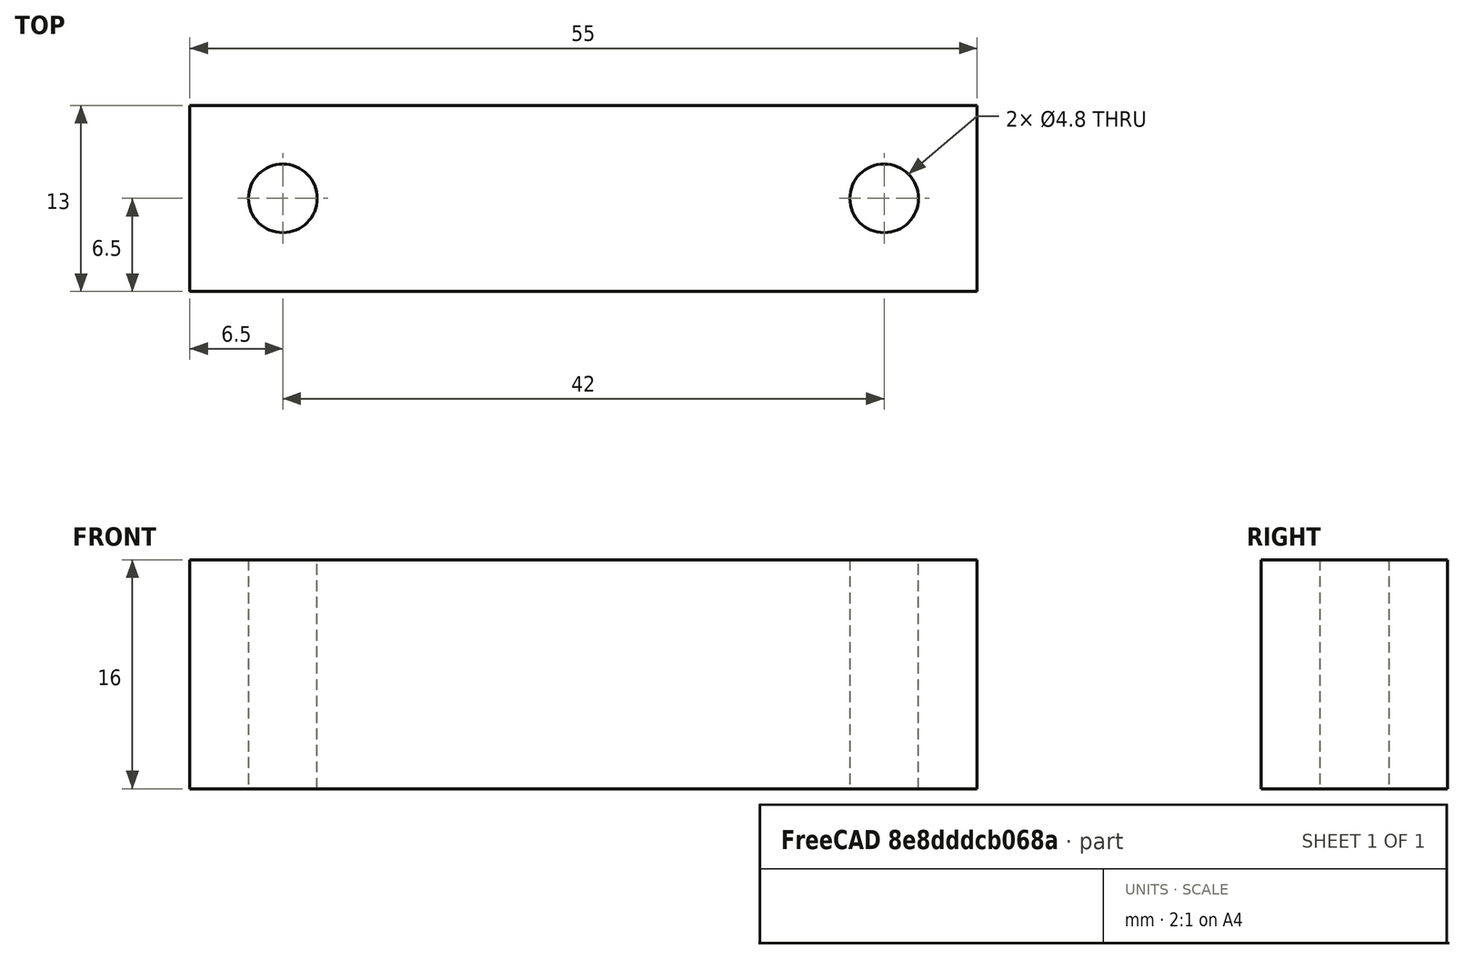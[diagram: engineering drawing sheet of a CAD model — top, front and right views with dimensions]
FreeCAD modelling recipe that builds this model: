
FCSTD DOCUMENT  (FreeCAD 0.16R6706 (Git))
Label: Calço Mancal Vertical
License: All rights reserved
LicenseURL: http://en.wikipedia.org/wiki/All_rights_reserved
objects: Sketcher::SketchObject×1, PartDesign::Pad×1
note: 3 computed .brp shape members not serialized (recipe doc carries the construction recipe); baked Part::Feature solids carry a one-line shape summary decoded from their .brp

FEATURE [Sketcher::SketchObject] Sketch
  sketch-geometry (6):
    g0: LineSegment StartX=-27.5 StartY=6.5 StartZ=0 EndX=27.5 EndY=6.5 EndZ=0
    g1: LineSegment StartX=27.5 StartY=6.5 StartZ=0 EndX=27.5 EndY=-6.5 EndZ=0
    g2: LineSegment StartX=27.5 StartY=-6.5 StartZ=0 EndX=-27.5 EndY=-6.5 EndZ=0
    g3: LineSegment StartX=-27.5 StartY=-6.5 StartZ=0 EndX=-27.5 EndY=6.5 EndZ=0
    g4: Circle CenterX=-21 CenterY=0 CenterZ=0 NormalX=0 NormalY=0 NormalZ=1 Radius=2.4
    g5: Circle CenterX=21 CenterY=0 CenterZ=0 NormalX=0 NormalY=0 NormalZ=1 Radius=2.4
  constraints (17):
    c: Coincident(g0,g1)
    c: Coincident(g1,g2)
    c: Coincident(g2,g3)
    c: Coincident(g3,g0)
    c: Horizontal(g0)
    c: Horizontal(g2)
    c: Vertical(g1)
    c: Vertical(g3)
    c: Symmetric(g2,g0,g-1)
    c: DistanceX(g2,g2) = 55
    c: DistanceY(g3,g3) = 13
    c: Radius(g4) = 2.4
    c: Equal(g4,g5) = 2.4
    c: PointOnObject(g4,g-1)
    c: PointOnObject(g5,g-1)
    c: DistanceX(g4,g5) = 42
    c: Symmetric(g4,g5,g-2)
FEATURE [PartDesign::Pad] Pad
  Length = 16
  Length2 = 100
  Sketch = -> Sketch
  Type = 0
